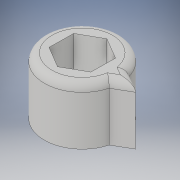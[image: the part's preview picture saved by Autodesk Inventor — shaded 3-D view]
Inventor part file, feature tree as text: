
AUTODESK INVENTOR PART (.ipt)
format: ipt  version: 2018.1 (Build 221171000, 171)  size: 138,240 bytes
history: native  units: in
note: dims shown in document units (in); Inventor stores cm internally (conversion verified against a paired STEP export)
features: sketch x4, extrude x3, fillet x2
ambient origin geometry x8: Origin, YZ Plane, XZ Plane, XY Plane, X Axis, Y Axis, Z Axis, Center Point
bodies: Solid1 (feature_tree)
feature tree (9):
  sketch  "Sketch1"  dims[d0=0.3937in d5=0.22in]
  sketch  "Sketch2"  dims[d6=0.2953in d7=0.0in d8=0.2953in d9=0.0in]
  sketch  "Sketch3"  dims[d10=0.2953in d11=0.0in d12=0.0394in d13=0.0394in]
  extrude  "Extrusion1"  Depth=0.3937in
  extrude  "Extrusion2"  Depth=0.2953in TaperAngle=0.0deg
  extrude  "Extrusion3"  Depth=0.0394in
  fillet  "Fillet1"  Radius=0.0394in
  fillet  "Fillet2"  [1 undecoded]
  sketch  "Sketch4"
note: 1 required parameter value undecoded (feature->parameter linkage not recoverable at this tier; creation-order binding heuristic only, values carry confidence <= 0.55)
